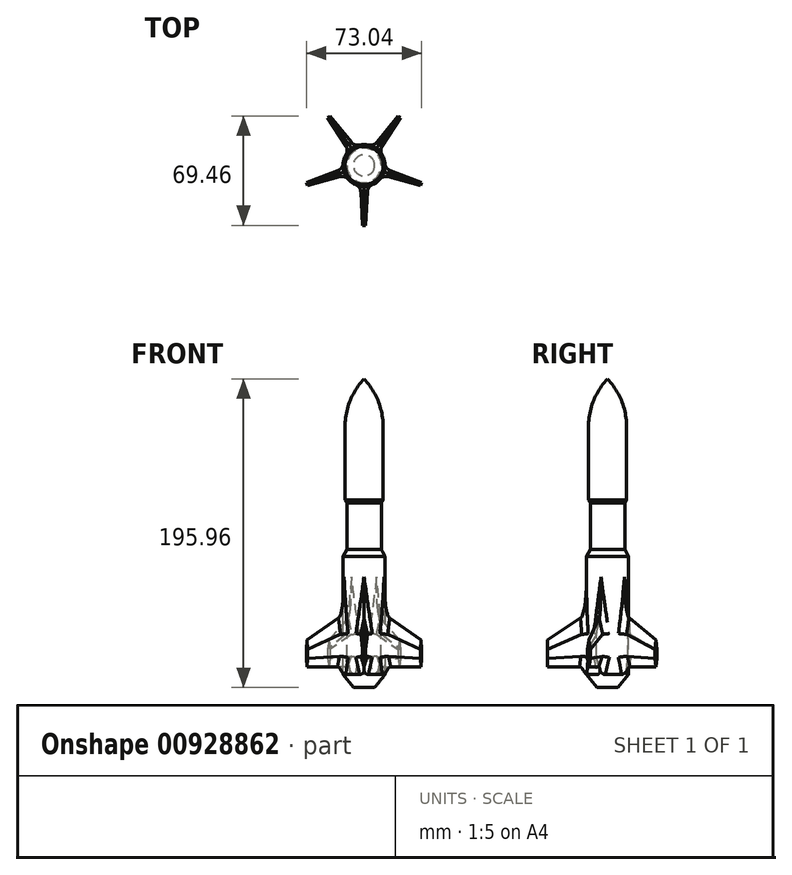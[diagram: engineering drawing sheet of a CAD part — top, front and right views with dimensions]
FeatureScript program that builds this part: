
annotation { "Feature Type Name" : "Feature", "Feature Type Description" : "" }
export const myFeature = defineFeature(function(context is Context, id is Id, definition is map)
    precondition{}
    {
        {
            var Q0;
            Q0=qCreatedBy(makeId("Front.planeOp"),FACE);
            cPlane(context, id + "F0", {"entities" : qUnion([Q0]), "cplaneType" : CPlaneType.OFFSET, "offset" : 12.7 * mm, "width" : 152.4 * mm, "height" : 152.4 * mm});
        }
        {
            var Q0;
            Q0=qCreatedBy(id+"F0.planeOp",FACE);
            var sketch = newSketch(context, id + "F1", { "sketchPlane" : qUnion([Q0])});
            skLineSegment(sketch, "E0", {"start": v(0, -13.73) * mm, "end": v(-2.3, -25.35) * mm});
            skLineSegment(sketch, "E1", {"start": v(-2.3, -25.35) * mm, "end": v(-2.3, -40.65) * mm});
            skLineSegment(sketch, "E2", {"start": v(-2.3, -40.65) * mm, "end": v(0, -47.66) * mm});
            skLineSegment(sketch, "E3.MirrorCS", {"start": v(0, -13.73) * mm, "end": v(2.3, -25.35) * mm});
            skLineSegment(sketch, "E4.MirrorCS", {"start": v(2.3, -25.35) * mm, "end": v(2.3, -40.65) * mm});
            skLineSegment(sketch, "E5.MirrorCS", {"start": v(2.3, -40.65) * mm, "end": v(0, -47.66) * mm});
            skSolve(sketch);
        }
        {
            var Q0;
            Q0=qCreatedBy(id+"F0.planeOp",FACE);
            cPlane(context, id + "F2", {"entities" : qUnion([Q0]), "cplaneType" : CPlaneType.OFFSET, "offset" : 25.4 * mm, "width" : 152.4 * mm, "height" : 152.4 * mm});
        }
        {
            var Q0;
            Q0=qCreatedBy(id+"F2.planeOp",FACE);
            var sketch = newSketch(context, id + "F3", { "sketchPlane" : qUnion([Q0])});
            skLineSegment(sketch, "E6", {"start": v(0, -30.7) * mm, "end": v(-0.92, -36.5) * mm});
            skLineSegment(sketch, "E7", {"start": v(-0.92, -36.5) * mm, "end": v(-0.92, -42.42) * mm});
            skLineSegment(sketch, "E8", {"start": v(-0.92, -42.42) * mm, "end": v(0, -47.57) * mm});
            skLineSegment(sketch, "E9.MirrorCS", {"start": v(0, -30.7) * mm, "end": v(0.92, -36.5) * mm});
            skLineSegment(sketch, "E10.MirrorCS", {"start": v(0.92, -36.5) * mm, "end": v(0.92, -42.42) * mm});
            skLineSegment(sketch, "E11.MirrorCS", {"start": v(0.92, -42.42) * mm, "end": v(0, -47.57) * mm});
            skSolve(sketch);
        }
        {
            var Q0;
            Q0=makeQuery(id+"F1.imprint","IMPRINT",FACE,{"disambiguationData":[TD([[makeQuery(id+"F1.imprint","IMPRINT",EDGE,{"derivedFrom":sQuery(id+"F1.wireOp",EDGE,"E0")}),1.0]])]});
            var Q1;
            Q1=makeQuery(id+"F3.imprint","IMPRINT",FACE,{"disambiguationData":[TD([[makeQuery(id+"F3.imprint","IMPRINT",EDGE,{"derivedFrom":sQuery(id+"F3.wireOp",EDGE,"E6")}),1.0]])]});
            loft(context, id + "F4", {"sheetProfilesArray" : [{ "sheetProfileEntities" : qUnion([Q0]) }, { "sheetProfileEntities" : qUnion([Q1]) }]});
        }
        {
            var Q0;
            Q0=qCreatedBy(makeId("Front.planeOp"),FACE);
            var sketch = newSketch(context, id + "F5", { "sketchPlane" : qUnion([Q0])});
            skLineSegment(sketch, "E12", {"start": v(0, 0) * mm, "end": v(0, -67.2) * mm});
            skSolve(sketch);
        }
        {
            var Q0;
            Q0=makeQuery(id+"F4.opLoft","SWEPT_BODY",BODY,{"disambiguationData":[OSD([makeQuery(id+"F1.imprint","IMPRINT",FACE,{"disambiguationData":[TD([[makeQuery(id+"F1.imprint","IMPRINT",EDGE,{"derivedFrom":sQuery(id+"F1.wireOp",EDGE,"E0")}),1.0]])]}),makeQuery(id+"F3.imprint","IMPRINT",FACE,{"disambiguationData":[TD([[makeQuery(id+"F3.imprint","IMPRINT",EDGE,{"derivedFrom":sQuery(id+"F3.wireOp",EDGE,"E6")}),1.0]])]})])]});
            var Q1;
            Q1=sQuery(id+"F5.wireOp",EDGE,"E12");
            circularPattern(context, id + "F6", {"entities" : qUnion([Q0]), "axis" : qUnion([Q1]), "angle" : 360 * degree, "instanceCount" : 5, "equalSpace" : true});
        }
        {
            var Q0;
            Q0=qCreatedBy(makeId("Front.planeOp"),FACE);
            var sketch = newSketch(context, id + "F7", { "sketchPlane" : qUnion([Q0])});
            skLineSegment(sketch, "E13", {"start": v(0, -60.74) * mm, "end": v(6.76, -60.74) * mm});
            skLineSegment(sketch, "E14", {"start": v(6.76, -60.74) * mm, "end": v(13.34, -52.52) * mm});
            skLineSegment(sketch, "E15", {"start": v(13.34, -52.52) * mm, "end": v(13.34, 22.34) * mm});
            skLineSegment(sketch, "E16", {"start": v(13.34, 22.34) * mm, "end": v(10.97, 27) * mm});
            skLineSegment(sketch, "E17", {"start": v(10.97, 27) * mm, "end": v(10.97, 56.5) * mm});
            skLineSegment(sketch, "E18", {"start": v(10.97, 56.5) * mm, "end": v(12.14, 58.47) * mm});
            skLineSegment(sketch, "E19", {"start": v(12.14, 58.47) * mm, "end": v(12.14, 104.7) * mm});
            skArc(sketch, "E20", {"start": v(12.14, 104.7) * mm, "mid": v(9, 121.13) * mm, "end": v(0, 135.22) * mm});
            skLineSegment(sketch, "E21", {"start": v(0, 135.22) * mm, "end": v(0, -60.74) * mm});
            skSolve(sketch);
        }
        {
            var Q0;
            Q0=makeQuery(id+"F7.imprint","IMPRINT",FACE,{"disambiguationData":[TD([[makeQuery(id+"F7.imprint","IMPRINT",EDGE,{"derivedFrom":sQuery(id+"F7.wireOp",EDGE,"E13")}),1.0]])]});
            var Q1;
            Q1=sQuery(id+"F7.wireOp",EDGE,"E21");
            revolve(context, id + "F8", {"surfaceOperationType" : NewSurfaceOperationType.NEW, "entities" : qUnion([Q0]), "axis" : qUnion([Q1]), "revolveType" : RevolveType.FULL});
        }
        {
            var Q0;
            Q0=makeQuery(id+"F8.opRevolve","SWEPT_BODY",BODY,{"disambiguationData":[OSD([sQuery(id+"F7.wireOp",EDGE,"E13"),sQuery(id+"F7.wireOp",EDGE,"E14"),sQuery(id+"F7.wireOp",EDGE,"E15"),sQuery(id+"F7.wireOp",EDGE,"E16"),sQuery(id+"F7.wireOp",EDGE,"E17"),sQuery(id+"F7.wireOp",EDGE,"E18"),sQuery(id+"F7.wireOp",EDGE,"E19"),sQuery(id+"F7.wireOp",EDGE,"E20"),sQuery(id+"F7.wireOp",EDGE,"E21")])]});
            var Q1;
            Q1=makeQuery(id+"F6.opPattern","COPY",BODY,{"derivedFrom":makeQuery(id+"F4.opLoft","SWEPT_BODY",BODY,{"disambiguationData":[OSD([makeQuery(id+"F1.imprint","IMPRINT",FACE,{"disambiguationData":[TD([[makeQuery(id+"F1.imprint","IMPRINT",EDGE,{"derivedFrom":sQuery(id+"F1.wireOp",EDGE,"E0")}),1.0]])]}),makeQuery(id+"F3.imprint","IMPRINT",FACE,{"disambiguationData":[TD([[makeQuery(id+"F3.imprint","IMPRINT",EDGE,{"derivedFrom":sQuery(id+"F3.wireOp",EDGE,"E6")}),1.0]])]})])]}),"instanceName":"1"});
            var Q2;
            Q2=makeQuery(id+"F4.opLoft","SWEPT_BODY",BODY,{"disambiguationData":[OSD([makeQuery(id+"F1.imprint","IMPRINT",FACE,{"disambiguationData":[TD([[makeQuery(id+"F1.imprint","IMPRINT",EDGE,{"derivedFrom":sQuery(id+"F1.wireOp",EDGE,"E0")}),1.0]])]}),makeQuery(id+"F3.imprint","IMPRINT",FACE,{"disambiguationData":[TD([[makeQuery(id+"F3.imprint","IMPRINT",EDGE,{"derivedFrom":sQuery(id+"F3.wireOp",EDGE,"E6")}),1.0]])]})])]});
            var Q3;
            Q3=makeQuery(id+"F6.opPattern","COPY",BODY,{"derivedFrom":makeQuery(id+"F4.opLoft","SWEPT_BODY",BODY,{"disambiguationData":[OSD([makeQuery(id+"F1.imprint","IMPRINT",FACE,{"disambiguationData":[TD([[makeQuery(id+"F1.imprint","IMPRINT",EDGE,{"derivedFrom":sQuery(id+"F1.wireOp",EDGE,"E0")}),1.0]])]}),makeQuery(id+"F3.imprint","IMPRINT",FACE,{"disambiguationData":[TD([[makeQuery(id+"F3.imprint","IMPRINT",EDGE,{"derivedFrom":sQuery(id+"F3.wireOp",EDGE,"E6")}),1.0]])]})])]}),"instanceName":"4"});
            var Q4;
            Q4=makeQuery(id+"F6.opPattern","COPY",BODY,{"derivedFrom":makeQuery(id+"F4.opLoft","SWEPT_BODY",BODY,{"disambiguationData":[OSD([makeQuery(id+"F1.imprint","IMPRINT",FACE,{"disambiguationData":[TD([[makeQuery(id+"F1.imprint","IMPRINT",EDGE,{"derivedFrom":sQuery(id+"F1.wireOp",EDGE,"E0")}),1.0]])]}),makeQuery(id+"F3.imprint","IMPRINT",FACE,{"disambiguationData":[TD([[makeQuery(id+"F3.imprint","IMPRINT",EDGE,{"derivedFrom":sQuery(id+"F3.wireOp",EDGE,"E6")}),1.0]])]})])]}),"instanceName":"3"});
            var Q5;
            Q5=makeQuery(id+"F6.opPattern","COPY",BODY,{"derivedFrom":makeQuery(id+"F4.opLoft","SWEPT_BODY",BODY,{"disambiguationData":[OSD([makeQuery(id+"F1.imprint","IMPRINT",FACE,{"disambiguationData":[TD([[makeQuery(id+"F1.imprint","IMPRINT",EDGE,{"derivedFrom":sQuery(id+"F1.wireOp",EDGE,"E0")}),1.0]])]}),makeQuery(id+"F3.imprint","IMPRINT",FACE,{"disambiguationData":[TD([[makeQuery(id+"F3.imprint","IMPRINT",EDGE,{"derivedFrom":sQuery(id+"F3.wireOp",EDGE,"E6")}),1.0]])]})])]}),"instanceName":"2"});
            booleanBodies(context, id + "F9", {"operationType" : BooleanOperationType.UNION, "tools" : qUnion([Q0, Q1, Q2, Q3, Q4, Q5])});
        }
        {
            var Q0;
            Q0=makeQuery(id+"F9.opBoolean","INTERSECT",EDGE,{"derivedFrom":[makeQuery(id+"F4.opLoft","SWEPT_FACE",FACE,{"disambiguationData":[OSD([sQuery(id+"F1.wireOp",EDGE,"E2"),sQuery(id+"F1.wireOp",EDGE,"E4.MirrorCS"),sQuery(id+"F1.wireOp",EDGE,"E5.MirrorCS"),sQuery(id+"F3.wireOp",EDGE,"E8"),sQuery(id+"F3.wireOp",EDGE,"E10.MirrorCS"),sQuery(id+"F3.wireOp",EDGE,"E11.MirrorCS")])]}),makeQuery(id+"F8.opRevolve","SWEPT_FACE",FACE,{"disambiguationData":[OSD([sQuery(id+"F7.wireOp",EDGE,"E15")])]})]});
            var Q1;
            Q1=makeQuery(id+"F9.opBoolean","INTERSECT",EDGE,{"derivedFrom":[makeQuery(id+"F4.opLoft","SWEPT_FACE",FACE,{"disambiguationData":[OSD([sQuery(id+"F1.wireOp",EDGE,"E3.MirrorCS"),sQuery(id+"F1.wireOp",EDGE,"E4.MirrorCS"),sQuery(id+"F1.wireOp",EDGE,"E5.MirrorCS"),sQuery(id+"F3.wireOp",EDGE,"E9.MirrorCS"),sQuery(id+"F3.wireOp",EDGE,"E10.MirrorCS"),sQuery(id+"F3.wireOp",EDGE,"E11.MirrorCS")])]}),makeQuery(id+"F8.opRevolve","SWEPT_FACE",FACE,{"disambiguationData":[OSD([sQuery(id+"F7.wireOp",EDGE,"E15")])]})]});
            var Q2;
            Q2=makeQuery(id+"F9.opBoolean","INTERSECT",EDGE,{"derivedFrom":[makeQuery(id+"F4.opLoft","SWEPT_FACE",FACE,{"disambiguationData":[OSD([sQuery(id+"F1.wireOp",EDGE,"E0"),sQuery(id+"F1.wireOp",EDGE,"E3.MirrorCS"),sQuery(id+"F1.wireOp",EDGE,"E4.MirrorCS"),sQuery(id+"F3.wireOp",EDGE,"E6"),sQuery(id+"F3.wireOp",EDGE,"E9.MirrorCS"),sQuery(id+"F3.wireOp",EDGE,"E10.MirrorCS")])]}),makeQuery(id+"F8.opRevolve","SWEPT_FACE",FACE,{"disambiguationData":[OSD([sQuery(id+"F7.wireOp",EDGE,"E15")])]})]});
            var Q3;
            Q3=makeQuery(id+"F9.opBoolean","INTERSECT",EDGE,{"derivedFrom":[makeQuery(id+"F6.opPattern","COPY",FACE,{"derivedFrom":makeQuery(id+"F4.opLoft","SWEPT_FACE",FACE,{"disambiguationData":[OSD([sQuery(id+"F1.wireOp",EDGE,"E1"),sQuery(id+"F1.wireOp",EDGE,"E2"),sQuery(id+"F1.wireOp",EDGE,"E5.MirrorCS"),sQuery(id+"F3.wireOp",EDGE,"E7"),sQuery(id+"F3.wireOp",EDGE,"E8"),sQuery(id+"F3.wireOp",EDGE,"E11.MirrorCS")])]}),"instanceName":"4"}),makeQuery(id+"F8.opRevolve","SWEPT_FACE",FACE,{"disambiguationData":[OSD([sQuery(id+"F7.wireOp",EDGE,"E15")])]})]});
            var Q4;
            Q4=makeQuery(id+"F9.opBoolean","INTERSECT",EDGE,{"derivedFrom":[makeQuery(id+"F6.opPattern","COPY",FACE,{"derivedFrom":makeQuery(id+"F4.opLoft","SWEPT_FACE",FACE,{"disambiguationData":[OSD([sQuery(id+"F1.wireOp",EDGE,"E0"),sQuery(id+"F1.wireOp",EDGE,"E1"),sQuery(id+"F1.wireOp",EDGE,"E2"),sQuery(id+"F3.wireOp",EDGE,"E6"),sQuery(id+"F3.wireOp",EDGE,"E7"),sQuery(id+"F3.wireOp",EDGE,"E8")])]}),"instanceName":"4"}),makeQuery(id+"F8.opRevolve","SWEPT_FACE",FACE,{"disambiguationData":[OSD([sQuery(id+"F7.wireOp",EDGE,"E15")])]})]});
            var Q5;
            Q5=makeQuery(id+"F9.opBoolean","INTERSECT",EDGE,{"derivedFrom":[makeQuery(id+"F6.opPattern","COPY",FACE,{"derivedFrom":makeQuery(id+"F4.opLoft","SWEPT_FACE",FACE,{"disambiguationData":[OSD([sQuery(id+"F1.wireOp",EDGE,"E0"),sQuery(id+"F1.wireOp",EDGE,"E1"),sQuery(id+"F1.wireOp",EDGE,"E3.MirrorCS"),sQuery(id+"F3.wireOp",EDGE,"E6"),sQuery(id+"F3.wireOp",EDGE,"E7"),sQuery(id+"F3.wireOp",EDGE,"E9.MirrorCS")])]}),"instanceName":"4"}),makeQuery(id+"F8.opRevolve","SWEPT_FACE",FACE,{"disambiguationData":[OSD([sQuery(id+"F7.wireOp",EDGE,"E15")])]})]});
            var Q6;
            Q6=makeQuery(id+"F9.opBoolean","INTERSECT",EDGE,{"derivedFrom":[makeQuery(id+"F6.opPattern","COPY",FACE,{"derivedFrom":makeQuery(id+"F4.opLoft","SWEPT_FACE",FACE,{"disambiguationData":[OSD([sQuery(id+"F1.wireOp",EDGE,"E2"),sQuery(id+"F1.wireOp",EDGE,"E4.MirrorCS"),sQuery(id+"F1.wireOp",EDGE,"E5.MirrorCS"),sQuery(id+"F3.wireOp",EDGE,"E8"),sQuery(id+"F3.wireOp",EDGE,"E10.MirrorCS"),sQuery(id+"F3.wireOp",EDGE,"E11.MirrorCS")])]}),"instanceName":"4"}),makeQuery(id+"F8.opRevolve","SWEPT_FACE",FACE,{"disambiguationData":[OSD([sQuery(id+"F7.wireOp",EDGE,"E15")])]})]});
            var Q7;
            Q7=makeQuery(id+"F9.opBoolean","INTERSECT",EDGE,{"derivedFrom":[makeQuery(id+"F6.opPattern","COPY",FACE,{"derivedFrom":makeQuery(id+"F4.opLoft","SWEPT_FACE",FACE,{"disambiguationData":[OSD([sQuery(id+"F1.wireOp",EDGE,"E3.MirrorCS"),sQuery(id+"F1.wireOp",EDGE,"E4.MirrorCS"),sQuery(id+"F1.wireOp",EDGE,"E5.MirrorCS"),sQuery(id+"F3.wireOp",EDGE,"E9.MirrorCS"),sQuery(id+"F3.wireOp",EDGE,"E10.MirrorCS"),sQuery(id+"F3.wireOp",EDGE,"E11.MirrorCS")])]}),"instanceName":"4"}),makeQuery(id+"F8.opRevolve","SWEPT_FACE",FACE,{"disambiguationData":[OSD([sQuery(id+"F7.wireOp",EDGE,"E15")])]})]});
            var Q8;
            Q8=makeQuery(id+"F9.opBoolean","INTERSECT",EDGE,{"derivedFrom":[makeQuery(id+"F6.opPattern","COPY",FACE,{"derivedFrom":makeQuery(id+"F4.opLoft","SWEPT_FACE",FACE,{"disambiguationData":[OSD([sQuery(id+"F1.wireOp",EDGE,"E0"),sQuery(id+"F1.wireOp",EDGE,"E3.MirrorCS"),sQuery(id+"F1.wireOp",EDGE,"E4.MirrorCS"),sQuery(id+"F3.wireOp",EDGE,"E6"),sQuery(id+"F3.wireOp",EDGE,"E9.MirrorCS"),sQuery(id+"F3.wireOp",EDGE,"E10.MirrorCS")])]}),"instanceName":"4"}),makeQuery(id+"F8.opRevolve","SWEPT_FACE",FACE,{"disambiguationData":[OSD([sQuery(id+"F7.wireOp",EDGE,"E15")])]})]});
            var Q9;
            Q9=makeQuery(id+"F9.opBoolean","INTERSECT",EDGE,{"derivedFrom":[makeQuery(id+"F6.opPattern","COPY",FACE,{"derivedFrom":makeQuery(id+"F4.opLoft","SWEPT_FACE",FACE,{"disambiguationData":[OSD([sQuery(id+"F1.wireOp",EDGE,"E0"),sQuery(id+"F1.wireOp",EDGE,"E1"),sQuery(id+"F1.wireOp",EDGE,"E3.MirrorCS"),sQuery(id+"F3.wireOp",EDGE,"E6"),sQuery(id+"F3.wireOp",EDGE,"E7"),sQuery(id+"F3.wireOp",EDGE,"E9.MirrorCS")])]}),"instanceName":"3"}),makeQuery(id+"F8.opRevolve","SWEPT_FACE",FACE,{"disambiguationData":[OSD([sQuery(id+"F7.wireOp",EDGE,"E15")])]})]});
            var Q10;
            Q10=makeQuery(id+"F9.opBoolean","INTERSECT",EDGE,{"derivedFrom":[makeQuery(id+"F6.opPattern","COPY",FACE,{"derivedFrom":makeQuery(id+"F4.opLoft","SWEPT_FACE",FACE,{"disambiguationData":[OSD([sQuery(id+"F1.wireOp",EDGE,"E0"),sQuery(id+"F1.wireOp",EDGE,"E1"),sQuery(id+"F1.wireOp",EDGE,"E2"),sQuery(id+"F3.wireOp",EDGE,"E6"),sQuery(id+"F3.wireOp",EDGE,"E7"),sQuery(id+"F3.wireOp",EDGE,"E8")])]}),"instanceName":"3"}),makeQuery(id+"F8.opRevolve","SWEPT_FACE",FACE,{"disambiguationData":[OSD([sQuery(id+"F7.wireOp",EDGE,"E15")])]})]});
            var Q11;
            Q11=makeQuery(id+"F9.opBoolean","INTERSECT",EDGE,{"derivedFrom":[makeQuery(id+"F6.opPattern","COPY",FACE,{"derivedFrom":makeQuery(id+"F4.opLoft","SWEPT_FACE",FACE,{"disambiguationData":[OSD([sQuery(id+"F1.wireOp",EDGE,"E1"),sQuery(id+"F1.wireOp",EDGE,"E2"),sQuery(id+"F1.wireOp",EDGE,"E5.MirrorCS"),sQuery(id+"F3.wireOp",EDGE,"E7"),sQuery(id+"F3.wireOp",EDGE,"E8"),sQuery(id+"F3.wireOp",EDGE,"E11.MirrorCS")])]}),"instanceName":"3"}),makeQuery(id+"F8.opRevolve","SWEPT_FACE",FACE,{"disambiguationData":[OSD([sQuery(id+"F7.wireOp",EDGE,"E15")])]})]});
            var Q12;
            Q12=makeQuery(id+"F9.opBoolean","INTERSECT",EDGE,{"derivedFrom":[makeQuery(id+"F6.opPattern","COPY",FACE,{"derivedFrom":makeQuery(id+"F4.opLoft","SWEPT_FACE",FACE,{"disambiguationData":[OSD([sQuery(id+"F1.wireOp",EDGE,"E2"),sQuery(id+"F1.wireOp",EDGE,"E4.MirrorCS"),sQuery(id+"F1.wireOp",EDGE,"E5.MirrorCS"),sQuery(id+"F3.wireOp",EDGE,"E8"),sQuery(id+"F3.wireOp",EDGE,"E10.MirrorCS"),sQuery(id+"F3.wireOp",EDGE,"E11.MirrorCS")])]}),"instanceName":"3"}),makeQuery(id+"F8.opRevolve","SWEPT_FACE",FACE,{"disambiguationData":[OSD([sQuery(id+"F7.wireOp",EDGE,"E15")])]})]});
            var Q13;
            Q13=makeQuery(id+"F9.opBoolean","INTERSECT",EDGE,{"derivedFrom":[makeQuery(id+"F6.opPattern","COPY",FACE,{"derivedFrom":makeQuery(id+"F4.opLoft","SWEPT_FACE",FACE,{"disambiguationData":[OSD([sQuery(id+"F1.wireOp",EDGE,"E3.MirrorCS"),sQuery(id+"F1.wireOp",EDGE,"E4.MirrorCS"),sQuery(id+"F1.wireOp",EDGE,"E5.MirrorCS"),sQuery(id+"F3.wireOp",EDGE,"E9.MirrorCS"),sQuery(id+"F3.wireOp",EDGE,"E10.MirrorCS"),sQuery(id+"F3.wireOp",EDGE,"E11.MirrorCS")])]}),"instanceName":"3"}),makeQuery(id+"F8.opRevolve","SWEPT_FACE",FACE,{"disambiguationData":[OSD([sQuery(id+"F7.wireOp",EDGE,"E15")])]})]});
            var Q14;
            Q14=makeQuery(id+"F9.opBoolean","INTERSECT",EDGE,{"derivedFrom":[makeQuery(id+"F6.opPattern","COPY",FACE,{"derivedFrom":makeQuery(id+"F4.opLoft","SWEPT_FACE",FACE,{"disambiguationData":[OSD([sQuery(id+"F1.wireOp",EDGE,"E0"),sQuery(id+"F1.wireOp",EDGE,"E3.MirrorCS"),sQuery(id+"F1.wireOp",EDGE,"E4.MirrorCS"),sQuery(id+"F3.wireOp",EDGE,"E6"),sQuery(id+"F3.wireOp",EDGE,"E9.MirrorCS"),sQuery(id+"F3.wireOp",EDGE,"E10.MirrorCS")])]}),"instanceName":"3"}),makeQuery(id+"F8.opRevolve","SWEPT_FACE",FACE,{"disambiguationData":[OSD([sQuery(id+"F7.wireOp",EDGE,"E15")])]})]});
            var Q15;
            Q15=makeQuery(id+"F9.opBoolean","INTERSECT",EDGE,{"derivedFrom":[makeQuery(id+"F6.opPattern","COPY",FACE,{"derivedFrom":makeQuery(id+"F4.opLoft","SWEPT_FACE",FACE,{"disambiguationData":[OSD([sQuery(id+"F1.wireOp",EDGE,"E1"),sQuery(id+"F1.wireOp",EDGE,"E2"),sQuery(id+"F1.wireOp",EDGE,"E5.MirrorCS"),sQuery(id+"F3.wireOp",EDGE,"E7"),sQuery(id+"F3.wireOp",EDGE,"E8"),sQuery(id+"F3.wireOp",EDGE,"E11.MirrorCS")])]}),"instanceName":"2"}),makeQuery(id+"F8.opRevolve","SWEPT_FACE",FACE,{"disambiguationData":[OSD([sQuery(id+"F7.wireOp",EDGE,"E15")])]})]});
            var Q16;
            Q16=makeQuery(id+"F9.opBoolean","INTERSECT",EDGE,{"derivedFrom":[makeQuery(id+"F6.opPattern","COPY",FACE,{"derivedFrom":makeQuery(id+"F4.opLoft","SWEPT_FACE",FACE,{"disambiguationData":[OSD([sQuery(id+"F1.wireOp",EDGE,"E0"),sQuery(id+"F1.wireOp",EDGE,"E1"),sQuery(id+"F1.wireOp",EDGE,"E2"),sQuery(id+"F3.wireOp",EDGE,"E6"),sQuery(id+"F3.wireOp",EDGE,"E7"),sQuery(id+"F3.wireOp",EDGE,"E8")])]}),"instanceName":"2"}),makeQuery(id+"F8.opRevolve","SWEPT_FACE",FACE,{"disambiguationData":[OSD([sQuery(id+"F7.wireOp",EDGE,"E15")])]})]});
            var Q17;
            Q17=makeQuery(id+"F9.opBoolean","INTERSECT",EDGE,{"derivedFrom":[makeQuery(id+"F6.opPattern","COPY",FACE,{"derivedFrom":makeQuery(id+"F4.opLoft","SWEPT_FACE",FACE,{"disambiguationData":[OSD([sQuery(id+"F1.wireOp",EDGE,"E0"),sQuery(id+"F1.wireOp",EDGE,"E1"),sQuery(id+"F1.wireOp",EDGE,"E3.MirrorCS"),sQuery(id+"F3.wireOp",EDGE,"E6"),sQuery(id+"F3.wireOp",EDGE,"E7"),sQuery(id+"F3.wireOp",EDGE,"E9.MirrorCS")])]}),"instanceName":"2"}),makeQuery(id+"F8.opRevolve","SWEPT_FACE",FACE,{"disambiguationData":[OSD([sQuery(id+"F7.wireOp",EDGE,"E15")])]})]});
            var Q18;
            Q18=makeQuery(id+"F9.opBoolean","INTERSECT",EDGE,{"derivedFrom":[makeQuery(id+"F6.opPattern","COPY",FACE,{"derivedFrom":makeQuery(id+"F4.opLoft","SWEPT_FACE",FACE,{"disambiguationData":[OSD([sQuery(id+"F1.wireOp",EDGE,"E2"),sQuery(id+"F1.wireOp",EDGE,"E4.MirrorCS"),sQuery(id+"F1.wireOp",EDGE,"E5.MirrorCS"),sQuery(id+"F3.wireOp",EDGE,"E8"),sQuery(id+"F3.wireOp",EDGE,"E10.MirrorCS"),sQuery(id+"F3.wireOp",EDGE,"E11.MirrorCS")])]}),"instanceName":"2"}),makeQuery(id+"F8.opRevolve","SWEPT_FACE",FACE,{"disambiguationData":[OSD([sQuery(id+"F7.wireOp",EDGE,"E15")])]})]});
            var Q19;
            Q19=makeQuery(id+"F9.opBoolean","INTERSECT",EDGE,{"derivedFrom":[makeQuery(id+"F6.opPattern","COPY",FACE,{"derivedFrom":makeQuery(id+"F4.opLoft","SWEPT_FACE",FACE,{"disambiguationData":[OSD([sQuery(id+"F1.wireOp",EDGE,"E3.MirrorCS"),sQuery(id+"F1.wireOp",EDGE,"E4.MirrorCS"),sQuery(id+"F1.wireOp",EDGE,"E5.MirrorCS"),sQuery(id+"F3.wireOp",EDGE,"E9.MirrorCS"),sQuery(id+"F3.wireOp",EDGE,"E10.MirrorCS"),sQuery(id+"F3.wireOp",EDGE,"E11.MirrorCS")])]}),"instanceName":"2"}),makeQuery(id+"F8.opRevolve","SWEPT_FACE",FACE,{"disambiguationData":[OSD([sQuery(id+"F7.wireOp",EDGE,"E15")])]})]});
            var Q20;
            Q20=makeQuery(id+"F9.opBoolean","INTERSECT",EDGE,{"derivedFrom":[makeQuery(id+"F6.opPattern","COPY",FACE,{"derivedFrom":makeQuery(id+"F4.opLoft","SWEPT_FACE",FACE,{"disambiguationData":[OSD([sQuery(id+"F1.wireOp",EDGE,"E0"),sQuery(id+"F1.wireOp",EDGE,"E3.MirrorCS"),sQuery(id+"F1.wireOp",EDGE,"E4.MirrorCS"),sQuery(id+"F3.wireOp",EDGE,"E6"),sQuery(id+"F3.wireOp",EDGE,"E9.MirrorCS"),sQuery(id+"F3.wireOp",EDGE,"E10.MirrorCS")])]}),"instanceName":"2"}),makeQuery(id+"F8.opRevolve","SWEPT_FACE",FACE,{"disambiguationData":[OSD([sQuery(id+"F7.wireOp",EDGE,"E15")])]})]});
            var Q21;
            Q21=makeQuery(id+"F9.opBoolean","INTERSECT",EDGE,{"derivedFrom":[makeQuery(id+"F6.opPattern","COPY",FACE,{"derivedFrom":makeQuery(id+"F4.opLoft","SWEPT_FACE",FACE,{"disambiguationData":[OSD([sQuery(id+"F1.wireOp",EDGE,"E1"),sQuery(id+"F1.wireOp",EDGE,"E2"),sQuery(id+"F1.wireOp",EDGE,"E5.MirrorCS"),sQuery(id+"F3.wireOp",EDGE,"E7"),sQuery(id+"F3.wireOp",EDGE,"E8"),sQuery(id+"F3.wireOp",EDGE,"E11.MirrorCS")])]}),"instanceName":"1"}),makeQuery(id+"F8.opRevolve","SWEPT_FACE",FACE,{"disambiguationData":[OSD([sQuery(id+"F7.wireOp",EDGE,"E15")])]})]});
            var Q22;
            Q22=makeQuery(id+"F9.opBoolean","INTERSECT",EDGE,{"derivedFrom":[makeQuery(id+"F6.opPattern","COPY",FACE,{"derivedFrom":makeQuery(id+"F4.opLoft","SWEPT_FACE",FACE,{"disambiguationData":[OSD([sQuery(id+"F1.wireOp",EDGE,"E0"),sQuery(id+"F1.wireOp",EDGE,"E1"),sQuery(id+"F1.wireOp",EDGE,"E2"),sQuery(id+"F3.wireOp",EDGE,"E6"),sQuery(id+"F3.wireOp",EDGE,"E7"),sQuery(id+"F3.wireOp",EDGE,"E8")])]}),"instanceName":"1"}),makeQuery(id+"F8.opRevolve","SWEPT_FACE",FACE,{"disambiguationData":[OSD([sQuery(id+"F7.wireOp",EDGE,"E15")])]})]});
            var Q23;
            Q23=makeQuery(id+"F9.opBoolean","INTERSECT",EDGE,{"derivedFrom":[makeQuery(id+"F6.opPattern","COPY",FACE,{"derivedFrom":makeQuery(id+"F4.opLoft","SWEPT_FACE",FACE,{"disambiguationData":[OSD([sQuery(id+"F1.wireOp",EDGE,"E0"),sQuery(id+"F1.wireOp",EDGE,"E1"),sQuery(id+"F1.wireOp",EDGE,"E3.MirrorCS"),sQuery(id+"F3.wireOp",EDGE,"E6"),sQuery(id+"F3.wireOp",EDGE,"E7"),sQuery(id+"F3.wireOp",EDGE,"E9.MirrorCS")])]}),"instanceName":"1"}),makeQuery(id+"F8.opRevolve","SWEPT_FACE",FACE,{"disambiguationData":[OSD([sQuery(id+"F7.wireOp",EDGE,"E15")])]})]});
            var Q24;
            Q24=makeQuery(id+"F9.opBoolean","INTERSECT",EDGE,{"derivedFrom":[makeQuery(id+"F6.opPattern","COPY",FACE,{"derivedFrom":makeQuery(id+"F4.opLoft","SWEPT_FACE",FACE,{"disambiguationData":[OSD([sQuery(id+"F1.wireOp",EDGE,"E2"),sQuery(id+"F1.wireOp",EDGE,"E4.MirrorCS"),sQuery(id+"F1.wireOp",EDGE,"E5.MirrorCS"),sQuery(id+"F3.wireOp",EDGE,"E8"),sQuery(id+"F3.wireOp",EDGE,"E10.MirrorCS"),sQuery(id+"F3.wireOp",EDGE,"E11.MirrorCS")])]}),"instanceName":"1"}),makeQuery(id+"F8.opRevolve","SWEPT_FACE",FACE,{"disambiguationData":[OSD([sQuery(id+"F7.wireOp",EDGE,"E15")])]})]});
            var Q25;
            Q25=makeQuery(id+"F9.opBoolean","INTERSECT",EDGE,{"derivedFrom":[makeQuery(id+"F6.opPattern","COPY",FACE,{"derivedFrom":makeQuery(id+"F4.opLoft","SWEPT_FACE",FACE,{"disambiguationData":[OSD([sQuery(id+"F1.wireOp",EDGE,"E3.MirrorCS"),sQuery(id+"F1.wireOp",EDGE,"E4.MirrorCS"),sQuery(id+"F1.wireOp",EDGE,"E5.MirrorCS"),sQuery(id+"F3.wireOp",EDGE,"E9.MirrorCS"),sQuery(id+"F3.wireOp",EDGE,"E10.MirrorCS"),sQuery(id+"F3.wireOp",EDGE,"E11.MirrorCS")])]}),"instanceName":"1"}),makeQuery(id+"F8.opRevolve","SWEPT_FACE",FACE,{"disambiguationData":[OSD([sQuery(id+"F7.wireOp",EDGE,"E15")])]})]});
            var Q26;
            Q26=makeQuery(id+"F9.opBoolean","INTERSECT",EDGE,{"derivedFrom":[makeQuery(id+"F6.opPattern","COPY",FACE,{"derivedFrom":makeQuery(id+"F4.opLoft","SWEPT_FACE",FACE,{"disambiguationData":[OSD([sQuery(id+"F1.wireOp",EDGE,"E0"),sQuery(id+"F1.wireOp",EDGE,"E3.MirrorCS"),sQuery(id+"F1.wireOp",EDGE,"E4.MirrorCS"),sQuery(id+"F3.wireOp",EDGE,"E6"),sQuery(id+"F3.wireOp",EDGE,"E9.MirrorCS"),sQuery(id+"F3.wireOp",EDGE,"E10.MirrorCS")])]}),"instanceName":"1"}),makeQuery(id+"F8.opRevolve","SWEPT_FACE",FACE,{"disambiguationData":[OSD([sQuery(id+"F7.wireOp",EDGE,"E15")])]})]});
            var Q27;
            Q27=makeQuery(id+"F9.opBoolean","INTERSECT",EDGE,{"derivedFrom":[makeQuery(id+"F4.opLoft","SWEPT_FACE",FACE,{"disambiguationData":[OSD([sQuery(id+"F1.wireOp",EDGE,"E1"),sQuery(id+"F1.wireOp",EDGE,"E2"),sQuery(id+"F1.wireOp",EDGE,"E5.MirrorCS"),sQuery(id+"F3.wireOp",EDGE,"E7"),sQuery(id+"F3.wireOp",EDGE,"E8"),sQuery(id+"F3.wireOp",EDGE,"E11.MirrorCS")])]}),makeQuery(id+"F8.opRevolve","SWEPT_FACE",FACE,{"disambiguationData":[OSD([sQuery(id+"F7.wireOp",EDGE,"E15")])]})]});
            var Q28;
            Q28=makeQuery(id+"F9.opBoolean","INTERSECT",EDGE,{"derivedFrom":[makeQuery(id+"F4.opLoft","SWEPT_FACE",FACE,{"disambiguationData":[OSD([sQuery(id+"F1.wireOp",EDGE,"E0"),sQuery(id+"F1.wireOp",EDGE,"E1"),sQuery(id+"F1.wireOp",EDGE,"E2"),sQuery(id+"F3.wireOp",EDGE,"E6"),sQuery(id+"F3.wireOp",EDGE,"E7"),sQuery(id+"F3.wireOp",EDGE,"E8")])]}),makeQuery(id+"F8.opRevolve","SWEPT_FACE",FACE,{"disambiguationData":[OSD([sQuery(id+"F7.wireOp",EDGE,"E15")])]})]});
            var Q29;
            Q29=makeQuery(id+"F9.opBoolean","INTERSECT",EDGE,{"derivedFrom":[makeQuery(id+"F4.opLoft","SWEPT_FACE",FACE,{"disambiguationData":[OSD([sQuery(id+"F1.wireOp",EDGE,"E0"),sQuery(id+"F1.wireOp",EDGE,"E1"),sQuery(id+"F1.wireOp",EDGE,"E3.MirrorCS"),sQuery(id+"F3.wireOp",EDGE,"E6"),sQuery(id+"F3.wireOp",EDGE,"E7"),sQuery(id+"F3.wireOp",EDGE,"E9.MirrorCS")])]}),makeQuery(id+"F8.opRevolve","SWEPT_FACE",FACE,{"disambiguationData":[OSD([sQuery(id+"F7.wireOp",EDGE,"E15")])]})]});
            fillet(context, id + "F10", {"entities" : qUnion([Q0, Q1, Q2, Q3, Q4, Q5, Q6, Q7, Q8, Q9, Q10, Q11, Q12, Q13, Q14, Q15, Q16, Q17, Q18, Q19, Q20, Q21, Q22, Q23, Q24, Q25, Q26, Q27, Q28, Q29]), "radius" : 5.08 * mm, "tangentPropagation" : true, "allowEdgeOverflow" : false});
        }
    });
